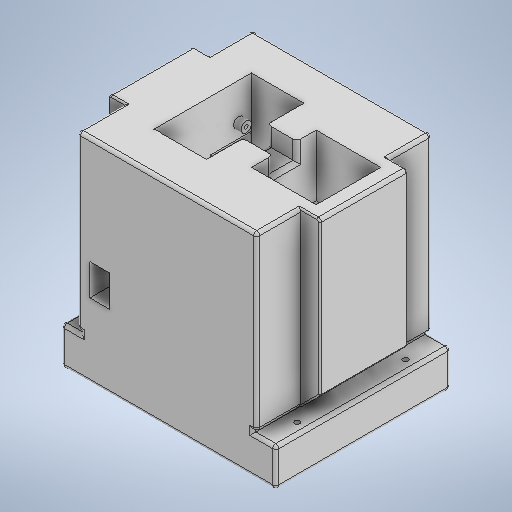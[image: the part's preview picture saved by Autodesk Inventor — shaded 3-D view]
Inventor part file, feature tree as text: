
AUTODESK INVENTOR PART (.ipt)
format: ipt  version: 2025 (Build 290162010, 162A)  size: 1,064,448 bytes
history: native  units: mm
features: fillet x39, extrude x29, sketch x22, projected_geometry x7, other x2, chamfer x2
ambient origin geometry x8: Origin, YZ Plane, XZ Plane, XY Plane, X Axis, Y Axis, Z Axis, Center Point
bodies: Solid1 (feature_tree)
feature tree (101):
  sketch  "Sketch1"  dims[d0=141.0mm d1=115.0mm]
  extrude  "Extrusion1"  Depth=115.0mm
  extrude  "Extrusion2"  Depth=21.0mm
  sketch  "Sketch3"  dims[d4=7.0mm d5=3.4mm]
  extrude  "Extrusion3"  Depth=3.4mm
  extrude  "Extrusion4"  Depth=3.4mm
  other  "Move Face2"
  extrude  "Extrusion5"  Depth=7.0mm
  other  "Move Face3"
  sketch  "Sketch9"  dims[d11=21.0mm d12=67.9mm]
  extrude  "Extrusion6"  Depth=67.9mm
  extrude  "Extrusion8"  Depth=21.0mm
  extrude  "Extrusion9"  Depth=127.0mm
  extrude  "Extrusion10"  Depth=17.0mm
  extrude  "Extrusion11"  Depth=17.0mm
  extrude  "Extrusion7"  Depth=25.5mm TaperAngle=0.0deg
  extrude  "Extrusion12"  Depth=12.6mm
  extrude  "Extrusion13"  Depth=8.0mm
  extrude  "Extrusion14"  Depth=8.0mm
  extrude  "Extrusion15"  Depth=12.6mm
  extrude  "Extrusion18"  Depth=34.0mm TaperAngle=0.0deg
  extrude  "Extrusion19"  Depth=67.5mm
  extrude  "Extrusion20"  Depth=18.0mm
  extrude  "Extrusion27"  Depth=42.5mm
  extrude  "Extrusion21"  Depth=36.25mm
  extrude  "Extrusion22"  Depth=20.0mm
  extrude  "Extrusion23"  Depth=21.25mm
  sketch  "Sketch10"  dims[d13=21.0mm d14=21.0mm]
  extrude  "Extrusion24"  Depth=21.25mm
  chamfer  "Chamfer1"  Distance=21.25mm
  chamfer  "Chamfer2"  Distance=3.0mm
  fillet  "Fillet1"  Radius=3.0mm
  fillet  "Fillet2"  Radius=31.0mm
  sketch  "Sketch22"  dims[d36=64.0mm d37=67.5mm]
  fillet  "Fillet3"  Radius=5.75mm
  fillet  "Fillet4"  Radius=5.75mm
  fillet  "Fillet5"  Radius=5.75mm
  fillet  "Fillet6"  Radius=53.800805mm
  fillet  "Fillet7"  Radius=75.050805mm
  fillet  "Fillet8"  Radius=3.0mm
  fillet  "Fillet9"  Radius=5.75mm
  fillet  "Fillet10"  Radius=5.75mm
  fillet  "Fillet11"  Radius=31.0mm
  fillet  "Fillet12"  Radius=3.0mm
  extrude  "Extrusion25"  Depth=31.0mm
  fillet  "Fillet27"  Radius=31.0mm
  fillet  "Fillet13"  Radius=5.75mm
  extrude  "Extrusion29"  Depth=5.75mm
  extrude  "Extrusion28"  Depth=3.998mm
  fillet  "Fillet14"  Radius=4.4mm
  extrude  "Extrusion30"  Depth=44.6mm TaperAngle=0.0deg
  fillet  "Fillet16"  Radius=25.0mm
  fillet  "Fillet17"  Radius=25.0mm
  fillet  "Fillet19"  Radius=25.0mm
  fillet  "Fillet21"  Radius=25.0mm
  fillet  "Fillet23"  Radius=55.2mm
  fillet  "Fillet38"  Radius=85.0mm
  fillet  "Fillet39"  Radius=64.0mm
  fillet  "Fillet40"  Radius=4.4mm
  fillet  "Fillet41"  Radius=4.4mm
  extrude  "Extrusion31"  Depth=6.8mm
  fillet  "Fillet43"  Radius=4.0mm
  fillet  "Fillet44"  Radius=4.0mm
  fillet  "Fillet24"  Radius=6.8mm
  fillet  "Fillet25"  Radius=4.0mm
  fillet  "Fillet26"  Radius=4.0mm
  fillet  "Fillet28"  Radius=6.8mm
  fillet  "Fillet29"  Radius=4.0mm
  extrude  "Extrusion26"  Depth=4.0mm
  fillet  "Fillet31"  Radius=6.8mm
  fillet  "Fillet32"  Radius=4.0mm
  fillet  "Fillet30"  Radius=4.0mm
  fillet  "Fillet33"  Radius=16.0mm
  fillet  "Fillet34"  Radius=12.0mm
  fillet  "Fillet35"  Radius=24.0mm
  fillet  "Fillet36"  Radius=24.0mm
  fillet  "Fillet37"  Radius=19.35mm
  sketch  "Sketch2"  dims[d2=3.4mm d3=21.0mm]
  projected_geometry  "Projected Loop1"
  sketch  "Sketch4"  dims[d6=3.4mm d7=3.4mm d8=7.0mm]
  projected_geometry  "Projected Loop2"
  sketch  "Sketch7"  dims[d9=7.0mm d10=7.0mm]
  projected_geometry  "Projected Loop4"
  projected_geometry  "Projected Loop5"
  projected_geometry  "Projected Loop6"
  projected_geometry  "Projected Loop7"
  projected_geometry  "Projected Loop8"
  sketch  "Sketch11"  dims[d15=69.6mm d16=127.0mm]
  sketch  "Sketch12"  dims[d17=127.0mm d18=17.0mm]
  sketch  "Sketch13"  dims[d19=25.0mm d20=17.0mm]
  sketch  "Sketch15"  dims[d21=26.0mm d22=25.5mm d23=0.0mm]
  sketch  "Sketch17"  dims[d24=12.6mm d25=12.6mm]
  sketch  "Sketch18"  dims[d26=1.7mm d27=0.0mm d28=8.0mm]
  sketch  "Sketch19"  dims[d29=8.0mm d30=8.0mm]
  sketch  "Sketch20"  dims[d31=8.0mm d32=12.6mm]
  sketch  "Sketch21"  dims[d33=10.6mm d34=34.0mm d35=0.0mm]
  sketch  "Sketch23"  dims[d38=21.0mm d39=0.0mm d47=18.0mm]
  sketch  "Sketch25"  dims[d48=13.6mm d49=0.0mm d60=42.5mm]
  sketch  "Sketch26"  dims[d62=115.0mm d63=36.25mm]
  sketch  "Sketch27"  dims[d64=36.25mm d65=20.0mm]
  sketch  "Sketch28"  dims[d66=21.25mm d67=21.25mm d68=21.25mm d69=21.25mm d71=3.0mm d72=3.0mm d76=31.0mm d78=5.75mm d81=5.75mm d82=5.75mm d83=53.800805mm d84=75.050805mm d85=3.0mm d86=5.75mm d87=5.75mm d88=31.0mm d89=3.0mm d90=31.0mm d91=31.0mm d92=5.75mm d93=5.75mm d94=3.998mm d95=4.4mm d96=0.0mm d97=44.6mm d98=0.0mm d99=25.0mm d100=0.0mm d101=25.0mm d102=0.0mm d103=25.0mm d104=0.0mm d105=25.0mm d106=0.0mm d107=55.2mm d108=85.0mm d109=64.0mm d110=4.4mm d111=4.4mm d112=6.8mm d113=4.0mm d114=4.0mm d115=6.8mm d116=4.0mm d117=4.0mm d118=6.8mm d119=4.0mm d120=4.0mm d121=6.8mm d122=4.0mm d123=4.0mm d124=16.0mm d125=12.0mm d126=24.0mm d127=24.0mm d129=19.35mm d130=0.0mm d131=12.9mm d132=20.68mm d133=49.26mm d134=8.25mm d135=40.0mm d136=0.0mm d137=2.0mm d138=0.0mm d139=40.0mm d140=0.0mm d151=3.638mm d152=0.0mm d153=1.0mm d154=0.0mm d155=12.0mm d156=18.0mm d157=87.2mm d158=25.5mm d159=10.6mm d160=10.15mm d161=14.0mm d163=36.0mm d164=36.0mm d165=50.0mm d166=0.0mm d167=22.0mm d168=4.0mm d169=0.0mm d170=0.2mm d171=0.0mm d172=0.2mm d173=0.0mm d174=0.2mm d175=0.0mm d176=2.0mm d177=2.0mm d178=1.0mm d179=1.0mm d180=1.0mm d181=1.0mm d182=2.0mm d183=2.0mm d184=2.0mm d185=2.0mm d186=2.0mm d187=2.0mm d188=3.0mm d189=2.0mm d191=4.0mm d192=3.0mm d194=2.0mm d196=2.5mm d198=6.0mm d199=2.0mm d200=1.0mm d201=1.0mm d202=4.5mm d204=30.28mm d205=11.5mm d206=0.0mm d207=2.0mm d208=10.6mm d209=2.0mm d210=45.0deg d211=12.6mm d212=2.0mm d213=45.0deg d214=1.0mm d215=1.0mm d217=1.0mm d218=0.0mm d219=0.0mm d220=2.0mm d221=2.0mm d222=0.5mm d223=2.0mm d224=2.0mm d225=0.0mm d226=2.0mm d227=9.5mm d228=0.0mm d229=0.0mm d230=2.0mm d231=2.0mm d232=2.0mm d233=8.0mm d234=5.5mm d235=20.0mm d236=0.0mm d237=45.0mm d238=20.0mm d239=2.5mm d240=2.5mm d241=2.5mm d242=2.5mm d243=5.0mm d244=0.0mm d245=10.0mm d246=0.0mm d247=5.0mm d248=0.0mm d249=29.2mm d250=1.9mm d251=2.5mm d252=1.9mm d253=2.5mm d254=120.0mm d255=0.0mm d256=2.0mm d257=2.0mm d258=2.0mm d259=5.0mm d260=2.0mm d261=10.0mm d262=2.0mm d263=10.98mm d264=4.0mm d265=0.0mm d267=2.0mm d268=2.0mm d50=0.872665mm d51=0.872665mm d145=0.5mm d146=0.872665mm d147=0.5mm d148=0.872665mm d149=0.5mm d150=0.872665mm d216=0.0mm d269=0.0mm d270=0.0mm d271=0.0mm d272=0.0mm]
